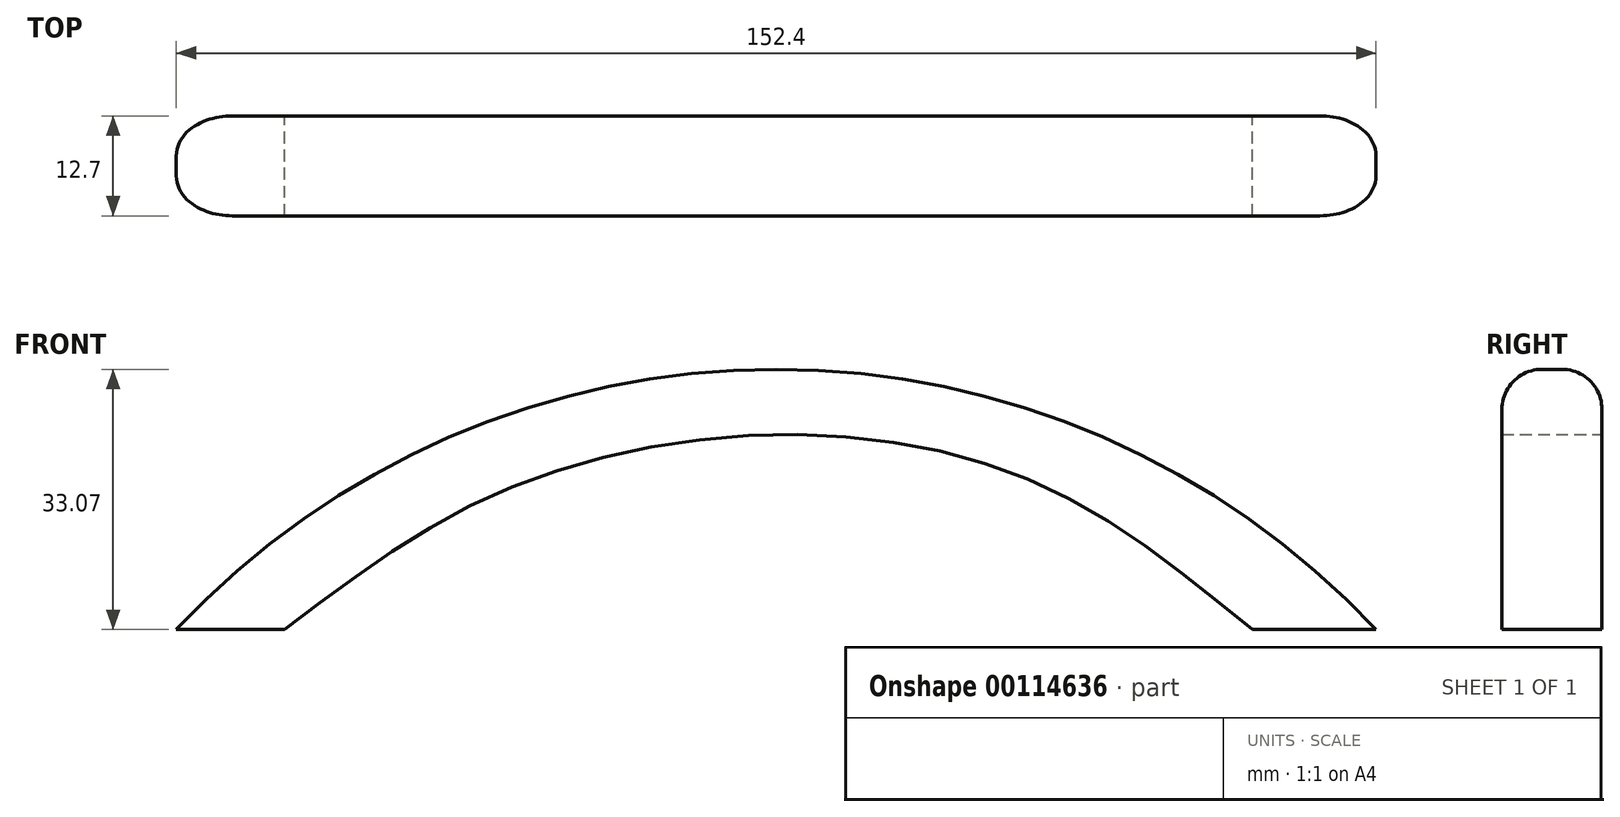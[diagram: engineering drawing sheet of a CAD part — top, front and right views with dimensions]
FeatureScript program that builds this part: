
annotation { "Feature Type Name" : "Feature", "Feature Type Description" : "" }
export const myFeature = defineFeature(function(context is Context, id is Id, definition is map)
    precondition{}
    {
        {
            var Q0;
            Q0=qCreatedBy(makeId("Front.planeOp"),FACE);
            var sketch = newSketch(context, id + "F0", { "sketchPlane" : qUnion([Q0])});
            skArc(sketch, "E0", {"start": v(76.2, 0) * mm, "mid": v(0, 33.07) * mm, "end": v(-76.2, 0) * mm});
            skFitSpline(sketch, "E1", {"points": [v(-62.44, 0) * mm, v(-35.96, 17.08) * mm, v(0, 24.76) * mm, v(34, 18.22) * mm, v(60.48, 0) * mm], "startDerivative": vector(102.51, 78.36) * mm, "endDerivative": vector(102.48, -84.44) * mm});
            skLineSegment(sketch, "E2", {"start": v(-76.2, 0) * mm, "end": v(-62.44, 0) * mm});
            skLineSegment(sketch, "E3", {"start": v(60.48, 0) * mm, "end": v(76.2, 0) * mm});
            skSolve(sketch);
        }
        {
            var Q0;
            Q0=makeQuery(id+"F0.imprint","IMPRINT",FACE,{"disambiguationData":[TD([[makeQuery(id+"F0.imprint","IMPRINT",EDGE,{"derivedFrom":sQuery(id+"F0.wireOp",EDGE,"E0")}),1.0]])]});
            extrude(context, id + "F1", {"entities" : qUnion([Q0]), "depth" : 12.7 * mm});
        }
        {
            var Q0;
            Q0=makeQuery(id+"F1.opExtrude","CAP_EDGE",EDGE,{"disambiguationData":[OSD([sQuery(id+"F0.wireOp",EDGE,"E0")])],"isStart":false});
            var Q1;
            Q1=makeQuery(id+"F1.opExtrude","CAP_EDGE",EDGE,{"disambiguationData":[OSD([sQuery(id+"F0.wireOp",EDGE,"E0")])],"isStart":true});
            fillet(context, id + "F2", {"entities" : qUnion([Q0, Q1]), "radius" : 5.08 * mm, "tangentPropagation" : true, "allowEdgeOverflow" : false});
        }
    });
